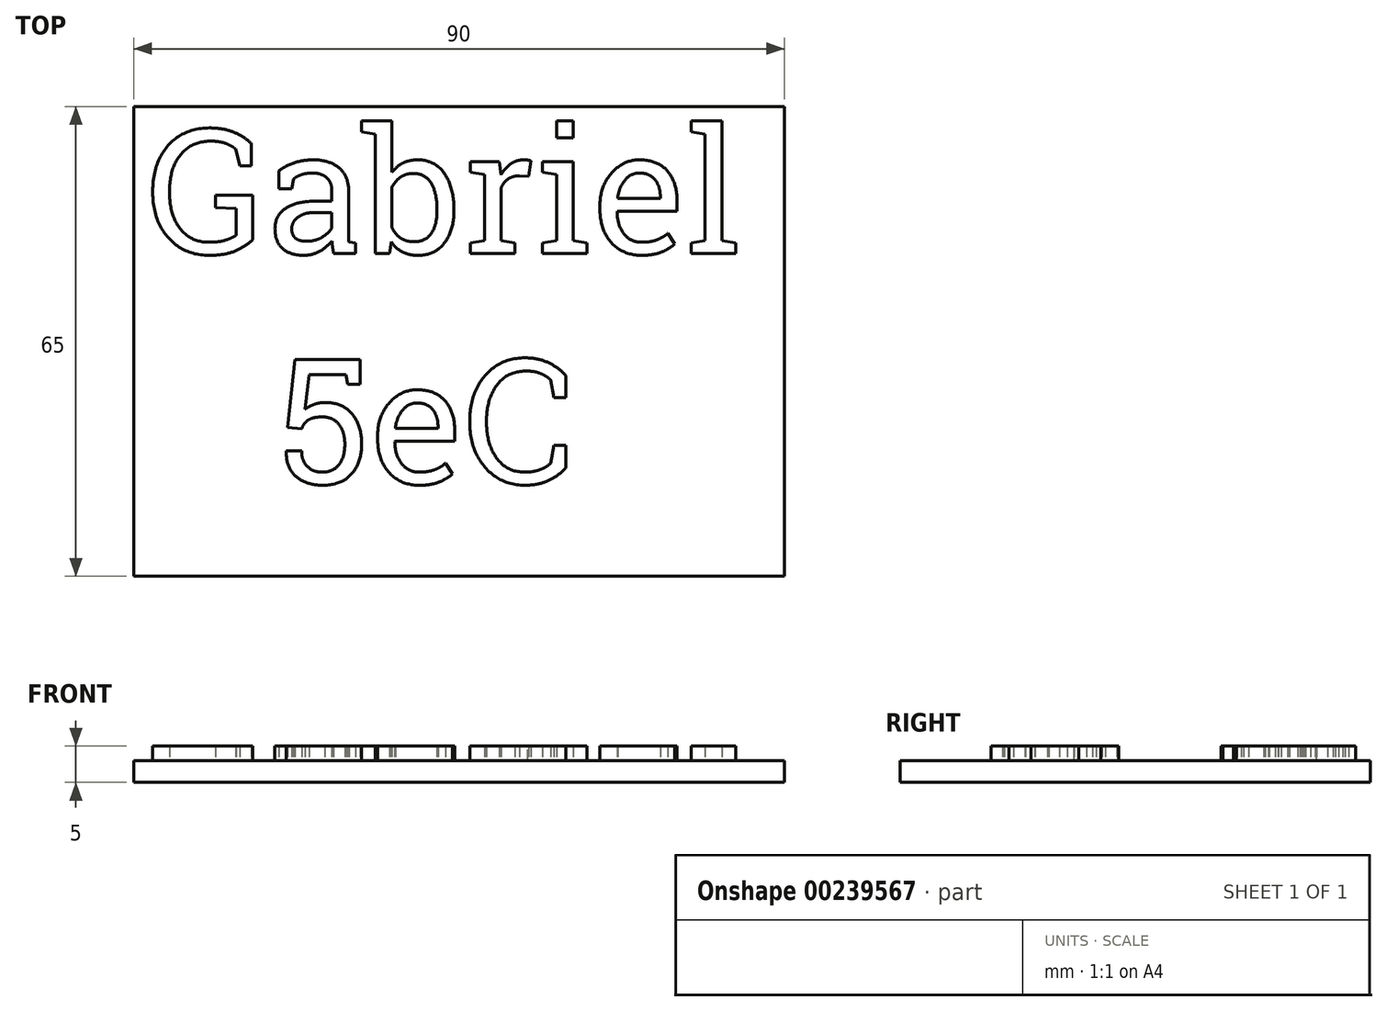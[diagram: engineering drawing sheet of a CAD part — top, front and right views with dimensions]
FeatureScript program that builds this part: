
annotation { "Feature Type Name" : "Feature", "Feature Type Description" : "" }
export const myFeature = defineFeature(function(context is Context, id is Id, definition is map)
    precondition{}
    {
        {
            var Q0;
            Q0=qCreatedBy(makeId("Top.planeOp"),FACE);
            var sketch = newSketch(context, id + "F0", { "sketchPlane" : qUnion([Q0])});
            skLineSegment(sketch, "E0.bottom", {"start": v(0, 0) * mm, "end": v(90, 0) * mm});
            skLineSegment(sketch, "E0.top", {"start": v(0, -65) * mm, "end": v(90, -65) * mm});
            skLineSegment(sketch, "E0.left", {"start": v(0, 0) * mm, "end": v(0, -65) * mm});
            skLineSegment(sketch, "E0.right", {"start": v(90, 0) * mm, "end": v(90, -65) * mm});
            skSolve(sketch);
        }
        {
            var Q0;
            Q0=makeQuery(id+"F0.imprint","IMPRINT",FACE,{"disambiguationData":[TD([[makeQuery(id+"F0.imprint","IMPRINT",EDGE,{"derivedFrom":sQuery(id+"F0.wireOp",EDGE,"E0.bottom")}),-1.0]])]});
            extrude(context, id + "F1", {"entities" : qUnion([Q0]), "depth" : 3 * mm});
        }
        {
            var Q0;
            Q0=makeQuery(id+"F1.opExtrude","CAP_FACE",FACE,{"disambiguationData":[OSD([sQuery(id+"F0.wireOp",EDGE,"E0.bottom"),sQuery(id+"F0.wireOp",EDGE,"E0.top"),sQuery(id+"F0.wireOp",EDGE,"E0.left"),sQuery(id+"F0.wireOp",EDGE,"E0.right")])],"isStart":false});
            var sketch = newSketch(context, id + "F2", { "sketchPlane" : qUnion([Q0])});
            skText(sketch, "E1", { "text": "Gabriel\n   5eC", "fontName": "RobotoSlab-Regular.ttf"});
            const initialGuessF2  = {"E1": [0.002, -0.02035, 1, 0, 0.01735]};
            skSetInitialGuess(sketch, initialGuessF2);
            skSolve(sketch);
        }
        {
            var Q0;
            Q0 = qSketchRegion(id + "F2", true);
            extrude(context, id + "F3", {"entities" : qUnion([Q0]), "operationType" : NewBodyOperationType.ADD, "depth" : 2 * mm});
        }
    });
